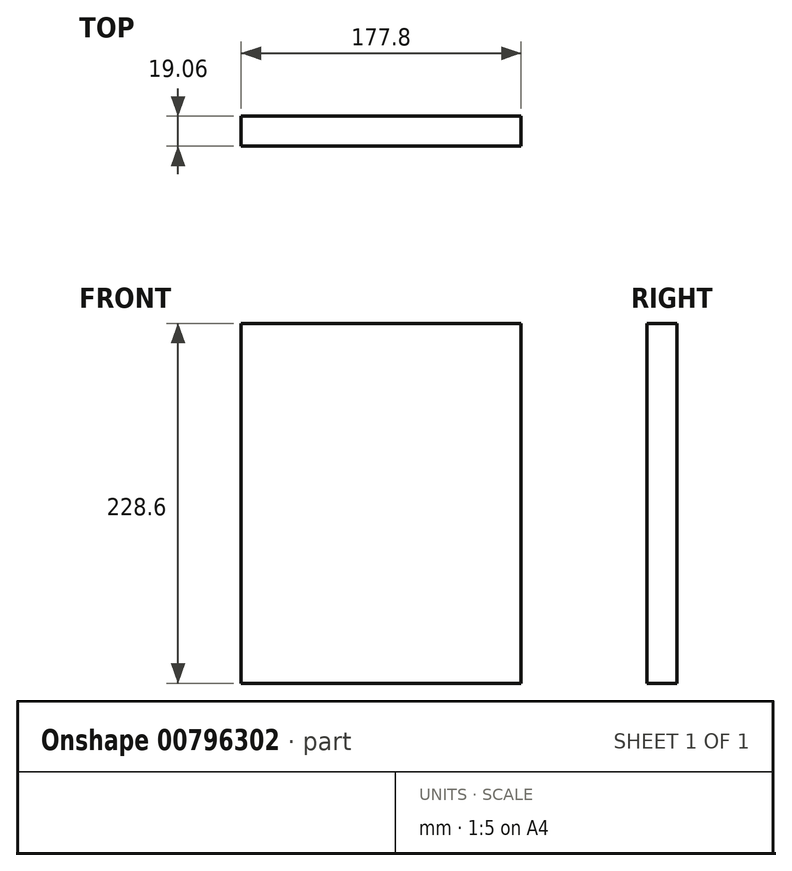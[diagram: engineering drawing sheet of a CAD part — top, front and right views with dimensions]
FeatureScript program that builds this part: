
annotation { "Feature Type Name" : "Feature", "Feature Type Description" : "" }
export const myFeature = defineFeature(function(context is Context, id is Id, definition is map)
    precondition{}
    {
        {
            var Q0;
            Q0=qCreatedBy(makeId("Front.planeOp"),FACE);
            var sketch = newSketch(context, id + "F0", { "sketchPlane" : qUnion([Q0])});
            skLineSegment(sketch, "E0.bottom", {"start": v(-88.9, 114.3) * mm, "end": v(88.9, 114.3) * mm});
            skLineSegment(sketch, "E0.top", {"start": v(-88.9, -114.3) * mm, "end": v(88.9, -114.3) * mm});
            skLineSegment(sketch, "E0.left", {"start": v(-88.9, 114.3) * mm, "end": v(-88.9, -114.3) * mm});
            skLineSegment(sketch, "E0.right", {"start": v(88.9, 114.3) * mm, "end": v(88.9, -114.3) * mm});
            skPoint(sketch, "E0.middle", {"position": v(0, 0) * mm});
            skSolve(sketch);
        }
        {
            var Q0;
            Q0 = qSketchRegion(id + "F0", true);
            extrude(context, id + "F1", {"entities" : qUnion([Q0]), "endBound" : BoundingType.SYMMETRIC, "depth" : 19.05 * mm, "offsetDistance" : 25.4 * mm});
        }
    });
